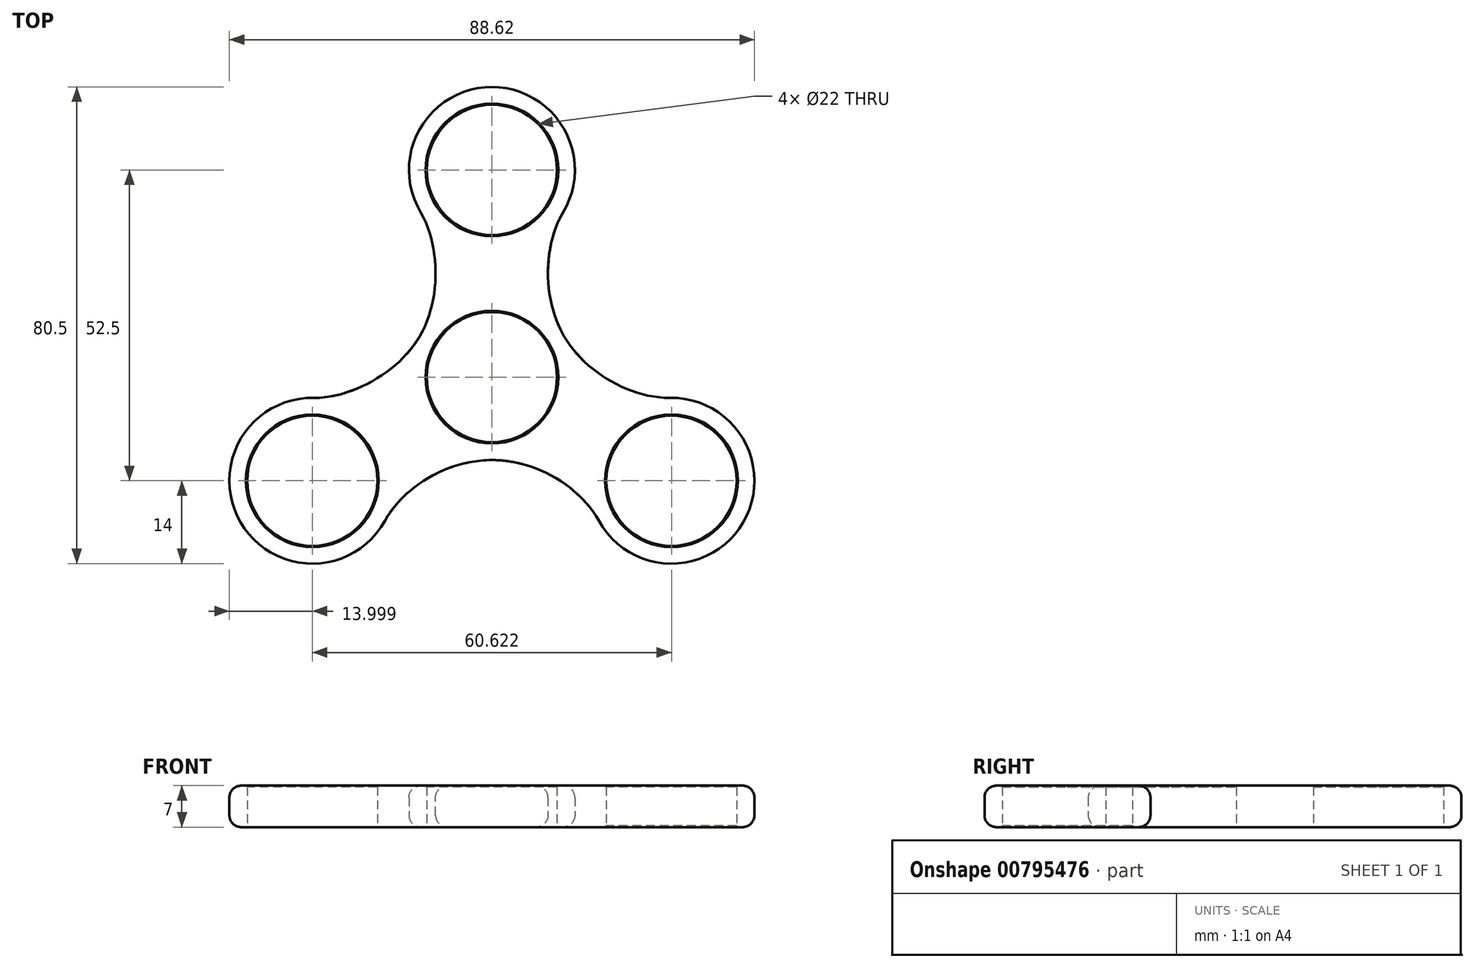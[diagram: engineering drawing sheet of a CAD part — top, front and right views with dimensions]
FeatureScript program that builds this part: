
annotation { "Feature Type Name" : "Feature", "Feature Type Description" : "" }
export const myFeature = defineFeature(function(context is Context, id is Id, definition is map)
    precondition{}
    {
        {
            var Q0;
            Q0=qCreatedBy(makeId("Top.planeOp"),FACE);
            var sketch = newSketch(context, id + "F0", { "sketchPlane" : qUnion([Q0])});
            skCircle(sketch, "E0", {"center": v(0, 0) * mm, "radius": 11 * mm});
            skLineSegment(sketch, "E1", {"start": v(0, 0) * mm, "end": v(0, 35) * mm});
            skLineSegment(sketch, "E2", {"start": v(0, 0) * mm, "end": v(-30.31, -17.5) * mm});
            skLineSegment(sketch, "E3", {"start": v(0, 0) * mm, "end": v(30.31, -17.5) * mm});
            skCircle(sketch, "E4", {"center": v(0, 35) * mm, "radius": 11 * mm});
            skCircle(sketch, "E5", {"center": v(-30.31, -17.5) * mm, "radius": 11 * mm});
            skCircle(sketch, "E6", {"center": v(30.31, -17.5) * mm, "radius": 11 * mm});
            skCircle(sketch, "E7", {"center": v(0, 35) * mm, "radius": 14 * mm});
            skCircle(sketch, "E8", {"center": v(-30.31, -17.5) * mm, "radius": 14 * mm});
            skCircle(sketch, "E9", {"center": v(30.31, -17.5) * mm, "radius": 14 * mm});
            skCircle(sketch, "E10", {"center": v(0, 0) * mm, "radius": 14 * mm});
            skFitSpline(sketch, "E11", {"points": [v(-12, 27.79) * mm, v(-12.12, 7) * mm, v(-30.07, -3.5) * mm], "startDerivative": vector(17.92, -29.83) * mm, "endDerivative": vector(-34.8, 0.6) * mm});
            skFitSpline(sketch, "E12", {"points": [v(12, 27.79) * mm, v(12.12, 7) * mm, v(30.07, -3.5) * mm], "startDerivative": vector(-18.97, -31.57) * mm, "endDerivative": vector(36.83, 0.64) * mm});
            skFitSpline(sketch, "E13", {"points": [v(-18.07, -24.29) * mm, v(0, -14) * mm, v(18.07, -24.29) * mm], "startDerivative": vector(19.56, 35.29) * mm, "endDerivative": vector(19.56, -35.29) * mm});
            skSolve(sketch);
        }
        {
            var Q0;
            Q0=makeQuery(id+"F0.imprint","IMPRINT",FACE,{"disambiguationData":[TD([[makeQuery(id+"F0.imprint","IMPRINT",EDGE,{"derivedFrom":sQuery(id+"F0.wireOp",EDGE,"E5")}),-1.0]])]});
            var Q1;
            {var subQ0=sQuery(id+"F0.wireOp",EDGE,"E2");var subQ1=sQuery(id+"F0.wireOp",EDGE,"E0");var subQ2=makeQuery(id+"F0.imprint","INTERSECT",VERTEX,{"derivedFrom":[subQ1,subQ0]});Q1=makeQuery(id+"F0.imprint","IMPRINT",FACE,{"disambiguationData":[TD([[makeQuery(id+"F0.imprint","IMPRINT",EDGE,{"disambiguationData":[TD([[subQ2,1.0]])],"derivedFrom":subQ1}),-1.0]])]});}
            var Q2;
            {var subQ0=sQuery(id+"F0.wireOp",EDGE,"E8");var subQ1=sQuery(id+"F0.wireOp",EDGE,"E2");var subQ2=makeQuery(id+"F0.imprint","INTERSECT",VERTEX,{"derivedFrom":[subQ1,subQ0]});Q2=makeQuery(id+"F0.imprint","IMPRINT",FACE,{"disambiguationData":[TD([[makeQuery(id+"F0.imprint","IMPRINT",EDGE,{"disambiguationData":[TD([[subQ2,1.0]])],"derivedFrom":subQ1}),-1.0]])]});}
            var Q3;
            {var subQ1=sQuery(id+"F0.wireOp",EDGE,"E0");var subQ6=sQuery(id+"F0.wireOp",EDGE,"E2");var subQ8=makeQuery(id+"F0.imprint","INTERSECT",VERTEX,{"derivedFrom":[subQ1,subQ6]});Q3=makeQuery(id+"F0.imprint","IMPRINT",FACE,{"disambiguationData":[TD([[makeQuery(id+"F0.imprint","IMPRINT",EDGE,{"disambiguationData":[TD([[subQ8,-1.0]])],"derivedFrom":subQ1}),-1.0]])]});}
            var Q4;
            {var subQ0=sQuery(id+"F0.wireOp",EDGE,"E8");var subQ1=sQuery(id+"F0.wireOp",EDGE,"E2");var subQ2=makeQuery(id+"F0.imprint","INTERSECT",VERTEX,{"derivedFrom":[subQ1,subQ0]});Q4=makeQuery(id+"F0.imprint","IMPRINT",FACE,{"disambiguationData":[TD([[makeQuery(id+"F0.imprint","IMPRINT",EDGE,{"disambiguationData":[TD([[subQ2,1.0]])],"derivedFrom":subQ1}),1.0]])]});}
            var Q5;
            {var subQ0=sQuery(id+"F0.wireOp",EDGE,"E9");var subQ1=sQuery(id+"F0.wireOp",EDGE,"E3");var subQ2=makeQuery(id+"F0.imprint","INTERSECT",VERTEX,{"derivedFrom":[subQ1,subQ0]});Q5=makeQuery(id+"F0.imprint","IMPRINT",FACE,{"disambiguationData":[TD([[makeQuery(id+"F0.imprint","IMPRINT",EDGE,{"disambiguationData":[TD([[subQ2,1.0]])],"derivedFrom":subQ1}),-1.0]])]});}
            var Q6;
            {var subQ1=sQuery(id+"F0.wireOp",EDGE,"E0");var subQ6=sQuery(id+"F0.wireOp",EDGE,"E1");var subQ8=makeQuery(id+"F0.imprint","INTERSECT",VERTEX,{"derivedFrom":[subQ1,subQ6]});Q6=makeQuery(id+"F0.imprint","IMPRINT",FACE,{"disambiguationData":[TD([[makeQuery(id+"F0.imprint","IMPRINT",EDGE,{"disambiguationData":[TD([[subQ8,1.0]])],"derivedFrom":subQ1}),-1.0]])]});}
            var Q7;
            Q7=makeQuery(id+"F0.imprint","IMPRINT",FACE,{"disambiguationData":[TD([[makeQuery(id+"F0.imprint","IMPRINT",EDGE,{"derivedFrom":sQuery(id+"F0.wireOp",EDGE,"E6")}),-1.0]])]});
            var Q8;
            {var subQ0=sQuery(id+"F0.wireOp",EDGE,"E9");var subQ1=sQuery(id+"F0.wireOp",EDGE,"E3");var subQ2=makeQuery(id+"F0.imprint","INTERSECT",VERTEX,{"derivedFrom":[subQ1,subQ0]});Q8=makeQuery(id+"F0.imprint","IMPRINT",FACE,{"disambiguationData":[TD([[makeQuery(id+"F0.imprint","IMPRINT",EDGE,{"disambiguationData":[TD([[subQ2,1.0]])],"derivedFrom":subQ1}),1.0]])]});}
            var Q9;
            {var subQ0=sQuery(id+"F0.wireOp",EDGE,"E7");var subQ1=sQuery(id+"F0.wireOp",EDGE,"E1");var subQ2=makeQuery(id+"F0.imprint","INTERSECT",VERTEX,{"derivedFrom":[subQ1,subQ0]});Q9=makeQuery(id+"F0.imprint","IMPRINT",FACE,{"disambiguationData":[TD([[makeQuery(id+"F0.imprint","IMPRINT",EDGE,{"disambiguationData":[TD([[subQ2,1.0]])],"derivedFrom":subQ1}),-1.0]])]});}
            var Q10;
            {var subQ0=sQuery(id+"F0.wireOp",EDGE,"E7");var subQ1=sQuery(id+"F0.wireOp",EDGE,"E1");var subQ2=makeQuery(id+"F0.imprint","INTERSECT",VERTEX,{"derivedFrom":[subQ1,subQ0]});Q10=makeQuery(id+"F0.imprint","IMPRINT",FACE,{"disambiguationData":[TD([[makeQuery(id+"F0.imprint","IMPRINT",EDGE,{"disambiguationData":[TD([[subQ2,1.0]])],"derivedFrom":subQ1}),1.0]])]});}
            var Q11;
            Q11=makeQuery(id+"F0.imprint","IMPRINT",FACE,{"disambiguationData":[TD([[makeQuery(id+"F0.imprint","IMPRINT",EDGE,{"derivedFrom":sQuery(id+"F0.wireOp",EDGE,"E4")}),-1.0]])]});
            extrude(context, id + "F1", {"entities" : qUnion([Q0, Q1, Q2, Q3, Q4, Q5, Q6, Q7, Q8, Q9, Q10, Q11]), "depth" : 7 * mm, "offsetDistance" : 25 * mm});
        }
        {
            var Q0;
            Q0=makeQuery(id+"F1.opExtrude","CAP_EDGE",EDGE,{"disambiguationData":[OSD([sQuery(id+"F0.wireOp",EDGE,"E8")])],"isStart":true});
            var Q1;
            Q1=makeQuery(id+"F1.opExtrude","CAP_EDGE",EDGE,{"disambiguationData":[OSD([sQuery(id+"F0.wireOp",EDGE,"E8")])],"isStart":false});
            fillet(context, id + "F2", {"entities" : qUnion([Q0, Q1]), "radius" : 2 * mm, "tangentPropagation" : true, "allowEdgeOverflow" : false});
        }
        {
            var Q0;
            Q0=makeQuery(id+"F1.opExtrude","CAP_EDGE",EDGE,{"disambiguationData":[OSD([sQuery(id+"F0.wireOp",EDGE,"E6")])],"isStart":true});
            chamfer(context, id + "F3", {"entities" : qUnion([Q0]), "width" : .2 * mm, "tangentPropagation" : true});
        }
        {
            var Q0;
            Q0=makeQuery(id+"F1.opExtrude","CAP_EDGE",EDGE,{"disambiguationData":[OSD([sQuery(id+"F0.wireOp",EDGE,"E5")])],"isStart":false});
            var Q1;
            Q1=makeQuery(id+"F1.opExtrude","CAP_EDGE",EDGE,{"disambiguationData":[OSD([sQuery(id+"F0.wireOp",EDGE,"E6")])],"isStart":false});
            var Q2;
            Q2=makeQuery(id+"F1.opExtrude","CAP_EDGE",EDGE,{"disambiguationData":[OSD([sQuery(id+"F0.wireOp",EDGE,"E4")])],"isStart":false});
            chamfer(context, id + "F4", {"entities" : qUnion([Q0, Q1, Q2]), "width" : .2 * mm, "tangentPropagation" : true});
        }
        {
            var Q0;
            Q0=makeQuery(id+"F1.opExtrude","CAP_EDGE",EDGE,{"disambiguationData":[OSD([sQuery(id+"F0.wireOp",EDGE,"E0")])],"isStart":false});
            chamfer(context, id + "F5", {"entities" : qUnion([Q0]), "width" : .2 * mm, "tangentPropagation" : true});
        }
    });
